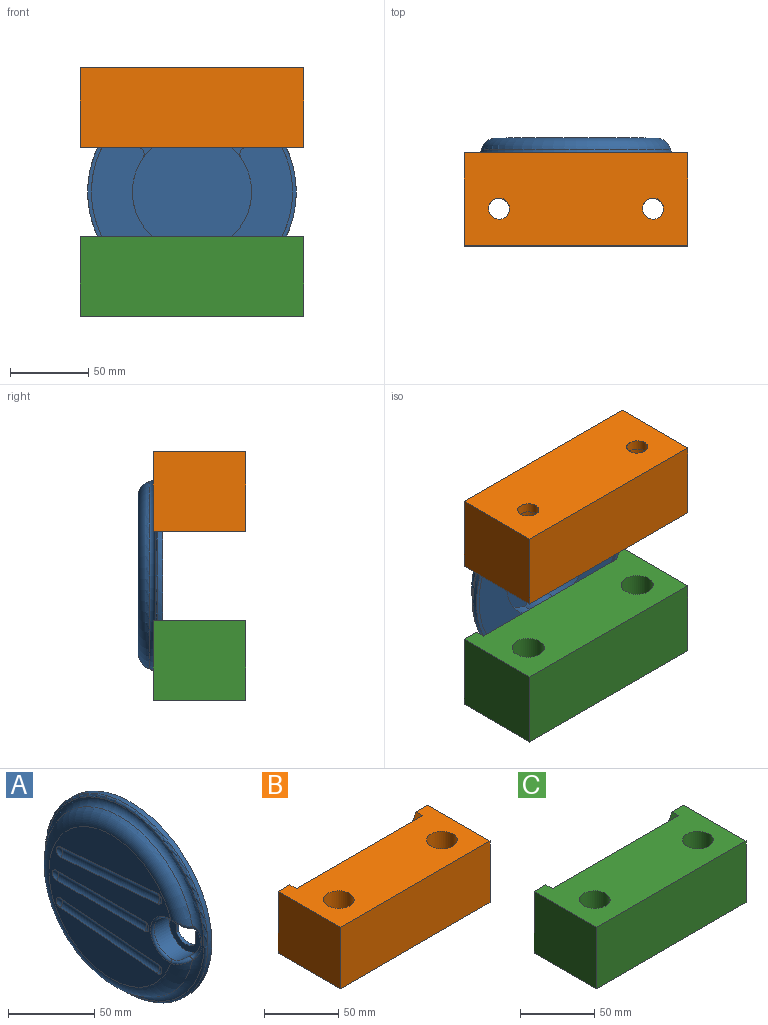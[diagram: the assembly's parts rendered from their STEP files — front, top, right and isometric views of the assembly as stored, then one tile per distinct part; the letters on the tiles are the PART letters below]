
ASSEMBLY  parts=3 mates=6
PART A: 78 faces, bbox 16.9x148.2x148.2 mm
  f0: cylinder r=1.6mm len=3.97mm, axis (1,0,0), area 10mm2, adj f1,f70,f71,f73
  f1: plane 22.2x3.97mm, normal (0,-1,0), area 88.1mm2, adj f0,f2,f70,f73
  f2: cylinder r=1.6mm len=3.97mm, axis (1,0,0), area 10mm2, adj f1,f70,f72,f73
  f3: plane 128.59x127.32mm, normal (1,0,0), area 6281.7mm2, adj f4,f5,f9,f11,f13,f14,f15,f23
  f4: plane 6.75x2.38mm, normal (0,-1,0), area 16.1mm2, adj f3,f7,f29,f71
  f5: plane 6.75x2.38mm, normal (0,1,0), area 16.1mm2, adj f3,f8,f29,f71
  f6: plane 6.78x0.06mm, normal (1,0,0), area 0.4mm2, adj f7,f8,f33,f71
  f7: cylinder r=2.38mm len=6.75mm, axis (0,0,1), area 25.2mm2, adj f4,f6,f33,f71
  f8: cylinder r=2.38mm len=6.75mm, axis (0,0,-1), area 25.2mm2, adj f5,f6,f33,f71
  f9: plane 25.4x3.18mm, normal (0,-1,0), area 80.6mm2, adj f3,f10,f40,f71
  f10: plane 25.4x11.51mm, normal (1,0,0), area 268.5mm2, adj f9,f11,f16,f40,f44,f71
  f11: cylinder r=38.1mm len=76.2mm, axis (1,0,0), area 2060.2mm2, adj f3,f10,f16,f17,f23,f42,f48,f49
  f12: plane 10.73x2.41mm, normal (1,0,0), area 25.9mm2, adj f13,f14,f54,f71
  f13: plane 10.73x3.18mm, normal (0,1,0), area 34.1mm2, adj f3,f12,f54,f71
  f14: plane 10.73x3.18mm, normal (0,-1,0), area 34.1mm2, adj f3,f12,f54,f71
  f15: plane 4.76x2.71mm, normal (0,1,0), area 12.9mm2, adj f3,f17,f40,f59
  f16: plane 17.8x1.59mm, normal (0,-1,0), area 28.3mm2, adj f10,f11,f17,f40
  f17: plane 17.8x10.75mm, normal (1,0,0), area 73.1mm2, adj f11,f15,f16,f40,f59
  f18: cylinder r=66.67mm len=133.35mm, axis (1,0,0), area 1330.1mm2, adj f22,f56
  f19: cylinder r=9.59mm len=15.95mm, axis (1,0,0), area 40.7mm2, adj f20,f25,f35,f57
  f20: plane 10.65x2.16mm, normal (0,-1,0), area 23mm2, adj f19,f21,f25,f57
  f21: cylinder r=9.59mm len=15.95mm, axis (1,0,0), area 40.7mm2, adj f20,f25,f35,f57
  f22: plane 133.35x133.35mm, normal (1,0,0), area 979.8mm2, adj f18,f24
  f23: cylinder r=15.08mm len=30.16mm, axis (1,0,0), area 404.2mm2, adj f3,f11,f25,f50
  f24: cylinder r=64.29mm len=128.59mm, axis (1,0,0), area 702.2mm2, adj f3,f22,f71,f72,f73
  f25: plane 30.16x30.16mm, normal (1,0,0), area 449mm2, adj f19,f20,f21,f23,f35
  f26: plane 6.75x2.38mm, normal (0,-1,0), area 16.1mm2, adj f3,f27,f31,f72
  f27: cylinder r=2.41mm len=4.83mm, axis (1,0,0), area 18.1mm2, adj f3,f26,f28,f32
  f28: plane 6.75x2.38mm, normal (0,1,0), area 16.1mm2, adj f3,f27,f34,f72
  f29: cylinder r=2.41mm len=4.83mm, axis (1,0,0), area 18.1mm2, adj f3,f4,f5,f33
  f30: plane 6.78x0.06mm, normal (1,0,0), area 0.4mm2, adj f31,f32,f34,f72
  f31: cylinder r=2.38mm len=6.75mm, axis (0,0,1), area 25.2mm2, adj f26,f30,f32,f72
  f32: torus R=0.03mm, axis (1,0,0), area 18.2mm2, adj f27,f30,f31,f34
  f33: torus R=0.03mm, axis (1,0,0), area 18.2mm2, adj f6,f7,f8,f29
  f34: cylinder r=2.38mm len=6.75mm, axis (0,0,-1), area 25.2mm2, adj f28,f30,f32,f72
  f35: plane 10.65x2.16mm, normal (0,1,0), area 23mm2, adj f19,f21,f25,f57
  f36: plane 102.31x99.93mm, normal (-1,0,0), area 5993mm2, adj f37,f61,f62,f63,f64,f65,f66,f67
  f37: torus R=51.16mm, axis (-1,0,0), area 4202.9mm2, adj f36,f38,f75,f76
  f38: torus R=65.09mm, axis (-1,0,0), area 2421.9mm2, adj f37,f56,f74
  f39: plane 14.81x4.76mm, normal (0,0,-1), area 52.3mm2, adj f3,f41,f42,f47,f48,f49
  f40: plane 14.81x4.76mm, normal (0,0,1), area 52.3mm2, adj f3,f9,f10,f15,f16,f17
  f41: plane 25.4x3.18mm, normal (0,-1,0), area 80.6mm2, adj f3,f39,f42,f72
  f42: plane 25.4x11.51mm, normal (1,0,0), area 268.5mm2, adj f11,f39,f41,f46,f48,f72
  f43: cone r=0mm half-angle=59deg, axis (1,0,0), area 10mm2, adj f44
  f44: cylinder r=1.65mm len=7.94mm, axis (1,0,0), area 82.3mm2, adj f10,f43
  f45: cone r=0mm half-angle=59deg, axis (1,0,0), area 10mm2, adj f46
  f46: cylinder r=1.65mm len=7.94mm, axis (1,0,0), area 82.3mm2, adj f42,f45
  f47: plane 4.76x2.71mm, normal (0,1,0), area 12.9mm2, adj f3,f39,f49,f60
  f48: plane 17.8x1.59mm, normal (0,-1,0), area 28.3mm2, adj f11,f39,f42,f49
  f49: plane 17.8x10.75mm, normal (1,0,0), area 73.1mm2, adj f11,f39,f47,f48,f60
  f50: plane 76.2x74.76mm, normal (1,0,0), area 4481.8mm2, adj f11,f23
  f51: plane 10.73x2.41mm, normal (1,0,0), area 25.9mm2, adj f52,f53,f55,f72
  f52: plane 10.73x3.18mm, normal (0,1,0), area 34.1mm2, adj f3,f51,f53,f72
  f53: plane 3.18x2.41mm, normal (0,0,-1), area 7.7mm2, adj f3,f51,f52,f55
  f54: plane 3.18x2.41mm, normal (0,0,1), area 7.7mm2, adj f3,f12,f13,f14
  f55: plane 10.73x3.18mm, normal (0,-1,0), area 34.1mm2, adj f3,f51,f53,f72
  f56: torus R=65.09mm, axis (-1,0,0), area 1035.6mm2, adj f18,f38
  f57: plane 27.78x27.78mm, normal (-1,0,0), area 340.6mm2, adj f19,f20,f21,f35,f58
  f58: cylinder r=13.89mm len=27.78mm, axis (1,0,0), area 791.8mm2, adj f57,f74,f75,f76,f77
  f59: cylinder r=4.76mm len=7.45mm, axis (1,0,0), area 49.2mm2, adj f3,f11,f15,f17
  f60: cylinder r=4.76mm len=7.45mm, axis (1,0,0), area 49.2mm2, adj f3,f11,f47,f49
  f61: sphere r=4.76mm, area 23.8mm2, adj f36,f62
  f62: cylinder r=4.76mm len=80.35mm, axis (0,-1,0.09), area 641.1mm2, adj f36,f61,f63
  f63: sphere r=4.76mm, area 23.8mm2, adj f36,f62
  f64: sphere r=4.76mm, area 23.8mm2, adj f36,f65
  f65: cylinder r=4.76mm len=72.19mm, axis (0,-1,0), area 578.3mm2, adj f36,f64,f66
  f66: sphere r=4.76mm, area 23.8mm2, adj f36,f65
  f67: cylinder r=4.76mm len=80.35mm, axis (0,-1,-0.09), area 641.1mm2, adj f36,f68,f69
  f68: sphere r=4.76mm, area 23.8mm2, adj f36,f67
  f69: sphere r=4.76mm, area 23.8mm2, adj f36,f67
  f70: plane 25.4x22.82mm, normal (1,0,0), area 541.3mm2, adj f0,f1,f2,f11,f71,f72
  f71: plane 27.11x6.35mm, normal (0,0,1), area 95.7mm2, adj f0,f3,f4,f5,f6,f7,f8,f9
  f72: plane 27.11x6.35mm, normal (0,0,-1), area 95.7mm2, adj f2,f3,f11,f24,f26,f28,f30,f31
  f73: plane 25.4x7.16mm, normal (1,0,0), area 131.5mm2, adj f0,f1,f2,f24,f71,f72
  f74: bspline ~24.41x7.08mm, area 86.6mm2, adj f38,f58,f75,f76
  f75: bspline ~13.54x8.92mm, area 41.9mm2, adj f37,f58,f74,f77
  f76: bspline ~13.54x8.93mm, area 41.9mm2, adj f37,f58,f74,f77
  f77: torus R=15.48mm, axis (-1,0,0), area 118.7mm2, adj f36,f58,f75,f76
PART B: 14 faces, bbox 142.9x59.4x50.8 mm
  f0: plane 59.36x50.8mm, normal (1,0,0), area 3015.5mm2, adj f1,f3,f4,f5
  f1: plane 142.88x50.8mm, normal (0,1,0), area 3965.4mm2, adj f0,f2,f4,f5,f12
  f2: plane 59.36x50.8mm, normal (-1,0,0), area 3015.5mm2, adj f1,f3,f4,f5
  f3: plane 142.88x50.8mm, normal (0,-1,0), area 7258mm2, adj f0,f2,f4,f5
  f4: plane 142.88x59.36mm, normal (0,0,-1), area 8195.1mm2, adj f0,f1,f2,f3,f6,f9
  f5: plane 142.88x59.36mm, normal (0,0,1), area 7047mm2, adj f0,f1,f2,f3,f8,f11,f12,f13
  f6: cylinder r=6.75mm len=13.49mm, axis (0,0,1), area 269.2mm2, adj f4,f7
  f7: plane 20.64x20.64mm, normal (0,0,1), area 191.5mm2, adj f6,f8
  f8: cylinder r=10.32mm len=44.45mm, axis (0,0,1), area 2881.9mm2, adj f5,f7
  f9: cylinder r=6.75mm len=13.49mm, axis (0,0,1), area 269.2mm2, adj f4,f10
  f10: plane 20.64x20.64mm, normal (0,0,1), area 191.5mm2, adj f9,f11
  f11: cylinder r=10.32mm len=44.45mm, axis (0,0,1), area 2881.9mm2, adj f5,f10
  f12: cylinder r=66.67mm len=120.48mm, axis (0,1,0), area 955.1mm2, adj f1,f5,f13
  f13: plane 120.48x38.1mm, normal (0,1,0), area 3292.7mm2, adj f5,f12
PART C: 23 faces, bbox 142.9x59.4x50.8 mm
  f0: plane 120.48x38.1mm, normal (0,1,0), area 3027.3mm2, adj f6,f13,f14,f15,f16,f17,f19,f20
  f1: plane 59.36x50.8mm, normal (1,0,0), area 3015.5mm2, adj f2,f4,f5,f6
  f2: plane 142.88x50.8mm, normal (0,1,0), area 3965.4mm2, adj f1,f3,f5,f6,f13
  f3: plane 59.36x50.8mm, normal (-1,0,0), area 3015.5mm2, adj f2,f4,f5,f6
  f4: plane 142.88x50.8mm, normal (0,-1,0), area 7258mm2, adj f1,f3,f5,f6
  f5: plane 142.88x59.36mm, normal (0,0,-1), area 8195.1mm2, adj f1,f2,f3,f4,f7,f10
  f6: plane 142.88x59.36mm, normal (0,0,1), area 7047mm2, adj f0,f1,f2,f3,f4,f9,f12,f13
  f7: cylinder r=6.75mm len=13.49mm, axis (0,0,1), area 269.2mm2, adj f5,f8
  f8: plane 20.64x20.64mm, normal (0,0,1), area 191.5mm2, adj f7,f9
  f9: cylinder r=10.32mm len=44.45mm, axis (0,0,1), area 2881.9mm2, adj f6,f8
  f10: cylinder r=6.75mm len=13.49mm, axis (0,0,1), area 269.2mm2, adj f5,f11
  f11: plane 20.64x20.64mm, normal (0,0,1), area 191.5mm2, adj f10,f12
  f12: cylinder r=10.32mm len=44.45mm, axis (0,0,1), area 2881.9mm2, adj f6,f11
  f13: cylinder r=66.67mm len=120.48mm, axis (0,1,0), area 955.1mm2, adj f0,f2,f6
  f14: plane 9.42x1.91mm, normal (0,0,1), area 17.9mm2, adj f0,f18,f19,f22
  f15: cylinder r=9.59mm len=15.15mm, axis (0,-1,0), area 33.3mm2, adj f0,f18,f19,f20
  f16: plane 9.42x1.91mm, normal (0,0,-1), area 17.9mm2, adj f0,f18,f20,f21
  f17: cylinder r=9.59mm len=15.15mm, axis (0,-1,0), area 33.3mm2, adj f0,f18,f21,f22
  f18: plane 19.18x15.95mm, normal (0,1,0), area 265.4mm2, adj f14,f15,f16,f17,f19,f20,f21,f22
  f19: cylinder r=1.91mm len=1.91mm, axis (0,-1,0), area 2.4mm2, adj f0,f14,f15,f18
  f20: cylinder r=1.91mm len=1.91mm, axis (0,-1,0), area 2.4mm2, adj f0,f15,f16,f18
  f21: cylinder r=1.91mm len=1.91mm, axis (0,-1,0), area 2.4mm2, adj f0,f16,f17,f18
  f22: cylinder r=1.91mm len=1.91mm, axis (0,-1,0), area 2.4mm2, adj f0,f14,f17,f18
PLACE A rot(axis=(0.58,-0.58,-0.58),120deg) t=(-2.36,-32.08,56.98)mm
PLACE B rot(axis=(0,1,0),180deg) t=(-2.36,-55.41,85.55)mm fixed
PLACE C t=(-2.36,-55.41,28.4)mm
MATE cylindrical B.f12 <-> A.f18  axis (0,1,0) through (-2.36,-28.91,56.98)mm
MATE parallel A.f20 <-> B.f9  axis (0,0,-1) through (-2.36,-31,17.33)mm
MATE cylindrical C.f7 <-> B.f9  axis (0,0,1) through (46.85,-61.47,6.18)mm
MATE cylindrical A.f18 <-> C.f13  axis (0,-1,0) through (-2.36,-30.49,56.98)mm
MATE planar B.f3 <-> C.f4  axis (0,-1,0) through (-2.36,-85.09,110.95)mm
MATE planar A.f18 <-> B.f13  axis (0,-1,0) through (-2.36,-32.08,56.98)mm
